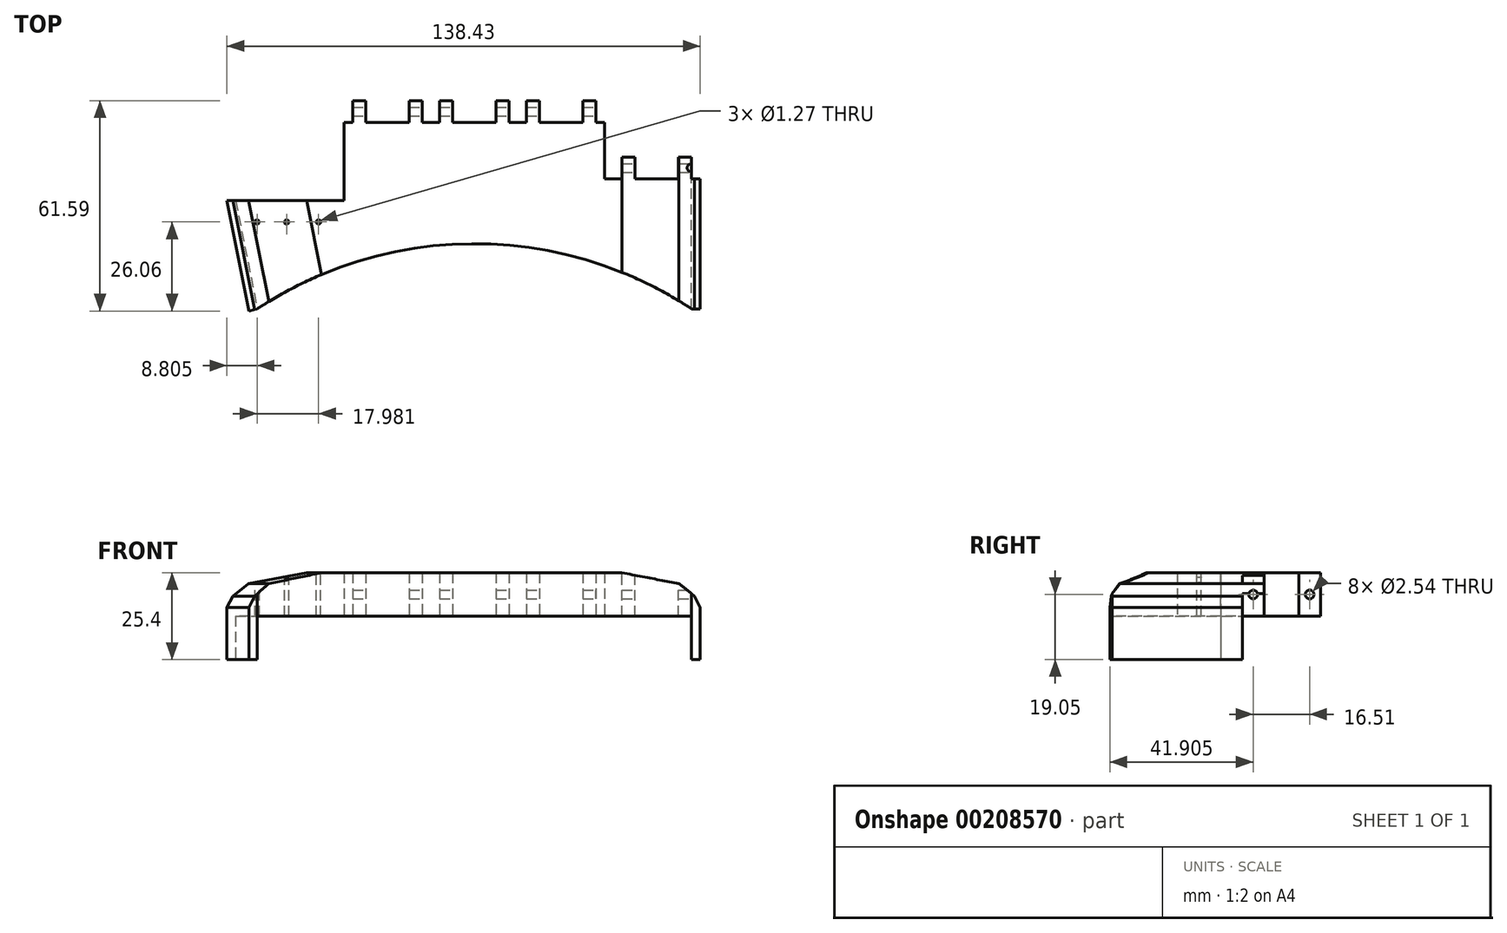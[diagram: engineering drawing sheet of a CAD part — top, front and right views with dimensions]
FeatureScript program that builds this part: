
annotation { "Feature Type Name" : "Feature", "Feature Type Description" : "" }
export const myFeature = defineFeature(function(context is Context, id is Id, definition is map)
    precondition{}
    {
        {
            var Q0;
            Q0=qCreatedBy(makeId("Top.planeOp"),FACE);
            var sketch = newSketch(context, id + "F0", { "sketchPlane" : qUnion([Q0])});
            skArc(sketch, "E0", {"start": v(63.5, 0) * mm, "mid": v(0, 19.05) * mm, "end": v(-63.5, 0) * mm});
            skPoint(sketch, "E1", {"position": v(-38.1, 0) * mm});
            skPoint(sketch, "E2", {"position": v(-38.1, 31.75) * mm});
            skLineSegment(sketch, "E3", {"start": v(-38.1, 31.75) * mm, "end": v(-69.85, 31.75) * mm});
            skLineSegment(sketch, "E4", {"start": v(-69.85, 31.75) * mm, "end": v(-63.5, 0) * mm});
            skLineSegment(sketch, "E5", {"start": v(63.5, 0) * mm, "end": v(63.5, 38.1) * mm});
            skLineSegment(sketch, "E6", {"start": v(63.5, 38.1) * mm, "end": v(38.1, 38.1) * mm});
            skLineSegment(sketch, "E7", {"start": v(38.1, 38.1) * mm, "end": v(38.1, 54.61) * mm});
            skLineSegment(sketch, "E8", {"start": v(38.1, 54.61) * mm, "end": v(-38.1, 54.61) * mm});
            skLineSegment(sketch, "E9", {"start": v(-38.1, 54.61) * mm, "end": v(-38.1, 31.75) * mm});
            skLineSegment(sketch, "E10", {"start": v(-69.85, 31.75) * mm, "end": v(-72.39, 31.75) * mm});
            skLineSegment(sketch, "E11", {"start": v(-72.39, 31.75) * mm, "end": v(-65.91, -0.63) * mm});
            skLineSegment(sketch, "E12", {"start": v(-63.5, 0) * mm, "end": v(-65.91, -0.63) * mm});
            skLineSegment(sketch, "E13", {"start": v(63.5, 38.1) * mm, "end": v(66.04, 38.1) * mm});
            skLineSegment(sketch, "E14", {"start": v(66.04, 0) * mm, "end": v(66.04, 38.1) * mm});
            skLineSegment(sketch, "E15", {"start": v(66.04, 0) * mm, "end": v(63.5, 0) * mm});
            skSolve(sketch);
        }
        {
            var Q0;
            Q0=makeQuery(id+"F0.imprint","IMPRINT",FACE,{"disambiguationData":[TD([[makeQuery(id+"F0.imprint","IMPRINT",EDGE,{"derivedFrom":sQuery(id+"F0.wireOp",EDGE,"E0")}),-1.0]])]});
            extrude(context, id + "F1", {"entities" : qUnion([Q0]), "depth" : 12.7 * mm});
        }
        {
            var Q0;
            Q0=makeQuery(id+"F0.imprint","IMPRINT",FACE,{"disambiguationData":[TD([[makeQuery(id+"F0.imprint","IMPRINT",EDGE,{"derivedFrom":sQuery(id+"F0.wireOp",EDGE,"E4")}),-1.0]])]});
            var Q1;
            Q1=makeQuery(id+"F0.imprint","IMPRINT",FACE,{"disambiguationData":[TD([[makeQuery(id+"F0.imprint","IMPRINT",EDGE,{"derivedFrom":sQuery(id+"F0.wireOp",EDGE,"E5")}),-1.0]])]});
            extrude(context, id + "F2", {"entities" : qUnion([Q0, Q1]), "operationType" : NewBodyOperationType.ADD, "endBound" : BoundingType.SYMMETRIC, "depth" : 25.4 * mm});
        }
        {
            var Q0;
            {var subQ0=sQuery(id+"F0.wireOp",EDGE,"E5");var subQ1=sQuery(id+"F0.wireOp",EDGE,"E4");Q0=makeQuery(id+"F2.boolean.opBoolean","MERGE",FACE,{"derivedFrom":[makeQuery(id+"F1.opExtrude","CAP_FACE",FACE,{"disambiguationData":[OSD([sQuery(id+"F0.wireOp",EDGE,"E0"),sQuery(id+"F0.wireOp",EDGE,"E3"),subQ1,subQ0,sQuery(id+"F0.wireOp",EDGE,"E6"),sQuery(id+"F0.wireOp",EDGE,"E7"),sQuery(id+"F0.wireOp",EDGE,"E8"),sQuery(id+"F0.wireOp",EDGE,"E9")])],"isStart":false}),makeQuery(id+"F2.opExtrude","CAP_FACE",FACE,{"disambiguationData":[OSD([subQ1,sQuery(id+"F0.wireOp",EDGE,"E10"),sQuery(id+"F0.wireOp",EDGE,"E11"),sQuery(id+"F0.wireOp",EDGE,"E12")])],"isStart":false}),makeQuery(id+"F2.opExtrude","CAP_FACE",FACE,{"disambiguationData":[OSD([subQ0,sQuery(id+"F0.wireOp",EDGE,"E13"),sQuery(id+"F0.wireOp",EDGE,"E14"),sQuery(id+"F0.wireOp",EDGE,"E15")])],"isStart":false})]});}
            var sketch = newSketch(context, id + "F3", { "sketchPlane" : qUnion([Q0])});
            skPoint(sketch, "E16", {"position": v(-63.58, 25.43) * mm});
            skPoint(sketch, "E17", {"position": v(-54.92, 25.43) * mm});
            skPoint(sketch, "E18", {"position": v(-45.6, 25.43) * mm});
            skLineSegment(sketch, "E19", {"start": v(-12.7, 54.61) * mm, "end": v(-12.7, 41.78) * mm});
            skLineSegment(sketch, "E20", {"start": v(12.7, 54.61) * mm, "end": v(12.7, 42.32) * mm});
            skLineSegment(sketch, "E21.bottom", {"start": v(-35.56, 54.61) * mm, "end": v(-30.48, 54.61) * mm});
            skLineSegment(sketch, "E21.top", {"start": v(-35.56, 44.45) * mm, "end": v(-30.48, 44.45) * mm});
            skLineSegment(sketch, "E21.left", {"start": v(-35.56, 54.61) * mm, "end": v(-35.56, 44.45) * mm});
            skLineSegment(sketch, "E21.right", {"start": v(-30.48, 54.61) * mm, "end": v(-30.48, 44.45) * mm});
            skLineSegment(sketch, "E22.bottom", {"start": v(-20.32, 54.61) * mm, "end": v(-15.24, 54.61) * mm});
            skLineSegment(sketch, "E22.top", {"start": v(-20.32, 44.45) * mm, "end": v(-15.24, 44.45) * mm});
            skLineSegment(sketch, "E22.left", {"start": v(-20.32, 54.61) * mm, "end": v(-20.32, 44.45) * mm});
            skLineSegment(sketch, "E22.right", {"start": v(-15.24, 54.61) * mm, "end": v(-15.24, 44.45) * mm});
            skLineSegment(sketch, "E23.MirrorCS", {"start": v(-5.08, 54.61) * mm, "end": v(-10.16, 54.61) * mm});
            skLineSegment(sketch, "E24.MirrorCS", {"start": v(-5.08, 44.45) * mm, "end": v(-10.16, 44.45) * mm});
            skLineSegment(sketch, "E25.MirrorCS", {"start": v(-5.08, 54.61) * mm, "end": v(-5.08, 44.45) * mm});
            skLineSegment(sketch, "E26.MirrorCS", {"start": v(5.08, 54.61) * mm, "end": v(5.08, 44.45) * mm});
            skLineSegment(sketch, "E27.MirrorCS", {"start": v(10.16, 54.61) * mm, "end": v(10.16, 44.45) * mm});
            skLineSegment(sketch, "E28.MirrorCS", {"start": v(10.16, 54.61) * mm, "end": v(5.08, 54.61) * mm});
            skLineSegment(sketch, "E29.MirrorCS", {"start": v(-10.16, 54.61) * mm, "end": v(-10.16, 44.45) * mm});
            skLineSegment(sketch, "E30.MirrorCS", {"start": v(10.16, 44.45) * mm, "end": v(5.08, 44.45) * mm});
            skLineSegment(sketch, "E31.MirrorCS", {"start": v(35.56, 54.61) * mm, "end": v(35.56, 44.45) * mm});
            skLineSegment(sketch, "E32.MirrorCS", {"start": v(30.48, 54.61) * mm, "end": v(30.48, 44.45) * mm});
            skLineSegment(sketch, "E33.MirrorCS", {"start": v(30.48, 44.45) * mm, "end": v(35.56, 44.45) * mm});
            skLineSegment(sketch, "E34.MirrorCS", {"start": v(15.24, 44.45) * mm, "end": v(20.32, 44.45) * mm});
            skLineSegment(sketch, "E35.MirrorCS", {"start": v(15.24, 54.61) * mm, "end": v(20.32, 54.61) * mm});
            skLineSegment(sketch, "E36.MirrorCS", {"start": v(20.32, 54.61) * mm, "end": v(20.32, 44.45) * mm});
            skLineSegment(sketch, "E37.MirrorCS", {"start": v(30.48, 54.61) * mm, "end": v(35.56, 54.61) * mm});
            skLineSegment(sketch, "E38.MirrorCS", {"start": v(15.24, 54.61) * mm, "end": v(15.24, 44.45) * mm});
            skLineSegment(sketch, "E39.MirrorCS", {"start": v(66.04, 38.1) * mm, "end": v(66.04, 27.94) * mm});
            skLineSegment(sketch, "E40.MirrorCS", {"start": v(60.96, 38.1) * mm, "end": v(60.96, 27.94) * mm});
            skLineSegment(sketch, "E41.MirrorCS", {"start": v(60.96, 27.94) * mm, "end": v(66.04, 27.94) * mm});
            skLineSegment(sketch, "E42.MirrorCS", {"start": v(45.72, 27.94) * mm, "end": v(50.8, 27.94) * mm});
            skLineSegment(sketch, "E43.MirrorCS", {"start": v(45.72, 38.1) * mm, "end": v(50.8, 38.1) * mm});
            skLineSegment(sketch, "E44.MirrorCS", {"start": v(50.8, 38.1) * mm, "end": v(50.8, 27.94) * mm});
            skLineSegment(sketch, "E45.MirrorCS", {"start": v(60.96, 38.1) * mm, "end": v(66.04, 38.1) * mm});
            skLineSegment(sketch, "E46.MirrorCS", {"start": v(45.72, 38.1) * mm, "end": v(45.72, 27.94) * mm});
            skSolve(sketch);
        }
        {
            var Q0;
            Q0=sQuery(id+"F3.wireOp",VERTEX,"E18");
            var Q1;
            Q1=sQuery(id+"F3.wireOp",VERTEX,"E17");
            var Q2;
            Q2=sQuery(id+"F3.wireOp",VERTEX,"E16");
            var Q3;
            Q3=makeQuery(id+"F1.opExtrude","SWEPT_BODY",BODY,{"disambiguationData":[OSD([sQuery(id+"F0.wireOp",EDGE,"E0"),sQuery(id+"F0.wireOp",EDGE,"E3"),sQuery(id+"F0.wireOp",EDGE,"E4"),sQuery(id+"F0.wireOp",EDGE,"E5"),sQuery(id+"F0.wireOp",EDGE,"E6"),sQuery(id+"F0.wireOp",EDGE,"E7"),sQuery(id+"F0.wireOp",EDGE,"E8"),sQuery(id+"F0.wireOp",EDGE,"E9")])]});
            hole(context, id + "F4", {"style" : HoleStyle.SIMPLE, "endStyle" : HoleEndStyle.THROUGH, "holeDiameter" : 1.27 * mm, "locations" : qUnion([Q0, Q1, Q2]), "scope" : qUnion([Q3]), "isTappedThrough" : true});
        }
        {
            var Q0;
            Q0=makeQuery(id+"F1.opExtrude","SWEPT_FACE",FACE,{"disambiguationData":[OSD([sQuery(id+"F0.wireOp",EDGE,"E8")])]});
            var sketch = newSketch(context, id + "F5", { "sketchPlane" : qUnion([Q0])});
            skLineSegment(sketch, "E47", {"start": v(12.7, 12.7) * mm, "end": v(12.7, 0) * mm});
            skLineSegment(sketch, "E48", {"start": v(-12.7, 12.7) * mm, "end": v(-12.7, 0) * mm});
            skLineSegment(sketch, "E49.bottom", {"start": v(-35.56, 12.7) * mm, "end": v(-31.75, 12.7) * mm});
            skLineSegment(sketch, "E49.top", {"start": v(-35.56, 0) * mm, "end": v(-31.75, 0) * mm});
            skLineSegment(sketch, "E49.left", {"start": v(-35.56, 12.7) * mm, "end": v(-35.56, 0) * mm});
            skLineSegment(sketch, "E49.right", {"start": v(-31.75, 12.7) * mm, "end": v(-31.75, 0) * mm});
            skLineSegment(sketch, "E50.bottom", {"start": v(-19.05, 12.7) * mm, "end": v(-15.24, 12.7) * mm});
            skLineSegment(sketch, "E50.top", {"start": v(-19.05, 0) * mm, "end": v(-15.24, 0) * mm});
            skLineSegment(sketch, "E50.left", {"start": v(-19.05, 12.7) * mm, "end": v(-19.05, 0) * mm});
            skLineSegment(sketch, "E50.right", {"start": v(-15.24, 12.7) * mm, "end": v(-15.24, 0) * mm});
            skLineSegment(sketch, "E51.MirrorCS", {"start": v(-6.35, 12.7) * mm, "end": v(-10.16, 12.7) * mm});
            skLineSegment(sketch, "E52.MirrorCS", {"start": v(10.16, 12.7) * mm, "end": v(6.35, 12.7) * mm});
            skLineSegment(sketch, "E53.MirrorCS", {"start": v(-6.35, 0) * mm, "end": v(-10.16, 0) * mm});
            skLineSegment(sketch, "E54.MirrorCS", {"start": v(10.16, 0) * mm, "end": v(6.35, 0) * mm});
            skLineSegment(sketch, "E55.MirrorCS", {"start": v(-6.35, 12.7) * mm, "end": v(-6.35, 0) * mm});
            skLineSegment(sketch, "E56.MirrorCS", {"start": v(10.16, 12.7) * mm, "end": v(10.16, 0) * mm});
            skLineSegment(sketch, "E57.MirrorCS", {"start": v(6.35, 12.7) * mm, "end": v(6.35, 0) * mm});
            skLineSegment(sketch, "E58.MirrorCS", {"start": v(-10.16, 12.7) * mm, "end": v(-10.16, 0) * mm});
            skLineSegment(sketch, "E59.MirrorCS", {"start": v(31.75, 0) * mm, "end": v(35.56, 0) * mm});
            skLineSegment(sketch, "E60.MirrorCS", {"start": v(15.24, 12.7) * mm, "end": v(19.05, 12.7) * mm});
            skLineSegment(sketch, "E61.MirrorCS", {"start": v(31.75, 12.7) * mm, "end": v(35.56, 12.7) * mm});
            skLineSegment(sketch, "E62.MirrorCS", {"start": v(15.24, 12.7) * mm, "end": v(15.24, 0) * mm});
            skLineSegment(sketch, "E63.MirrorCS", {"start": v(31.75, 12.7) * mm, "end": v(31.75, 0) * mm});
            skLineSegment(sketch, "E64.MirrorCS", {"start": v(15.24, 0) * mm, "end": v(19.05, 0) * mm});
            skLineSegment(sketch, "E65.MirrorCS", {"start": v(19.05, 12.7) * mm, "end": v(19.05, 0) * mm});
            skLineSegment(sketch, "E66.MirrorCS", {"start": v(35.56, 12.7) * mm, "end": v(35.56, 0) * mm});
            skSolve(sketch);
        }
        {
            var Q0;
            Q0=makeQuery(id+"F5.imprint","IMPRINT",FACE,{"disambiguationData":[TD([[makeQuery(id+"F5.imprint","IMPRINT",EDGE,{"derivedFrom":sQuery(id+"F5.wireOp",EDGE,"E49.bottom")}),-1.0]])]});
            var Q1;
            Q1=makeQuery(id+"F5.imprint","IMPRINT",FACE,{"disambiguationData":[TD([[makeQuery(id+"F5.imprint","IMPRINT",EDGE,{"derivedFrom":sQuery(id+"F5.wireOp",EDGE,"E50.bottom")}),-1.0]])]});
            var Q2;
            Q2=makeQuery(id+"F5.imprint","IMPRINT",FACE,{"disambiguationData":[TD([[makeQuery(id+"F5.imprint","IMPRINT",EDGE,{"derivedFrom":sQuery(id+"F5.wireOp",EDGE,"E51.MirrorCS")}),-1.0]])]});
            var Q3;
            Q3=makeQuery(id+"F5.imprint","IMPRINT",FACE,{"disambiguationData":[TD([[makeQuery(id+"F5.imprint","IMPRINT",EDGE,{"derivedFrom":sQuery(id+"F5.wireOp",EDGE,"E52.MirrorCS")}),-1.0]])]});
            var Q4;
            Q4=makeQuery(id+"F5.imprint","IMPRINT",FACE,{"disambiguationData":[TD([[makeQuery(id+"F5.imprint","IMPRINT",EDGE,{"derivedFrom":sQuery(id+"F5.wireOp",EDGE,"E60.MirrorCS")}),-1.0]])]});
            var Q5;
            Q5=makeQuery(id+"F5.imprint","IMPRINT",FACE,{"disambiguationData":[TD([[makeQuery(id+"F5.imprint","IMPRINT",EDGE,{"derivedFrom":sQuery(id+"F5.wireOp",EDGE,"E59.MirrorCS")}),1.0]])]});
            extrude(context, id + "F6", {"entities" : qUnion([Q0, Q1, Q2, Q3, Q4, Q5]), "operationType" : NewBodyOperationType.ADD, "depth" : 6.35 * mm});
        }
        {
            var Q0;
            Q0=makeQuery(id+"F6.opExtrude","SWEPT_FACE",FACE,{"disambiguationData":[OSD([sQuery(id+"F5.wireOp",EDGE,"E49.left")])]});
            var sketch = newSketch(context, id + "F7", { "sketchPlane" : qUnion([Q0])});
            skPoint(sketch, "E67", {"position": v(57.79, 6.35) * mm});
            skPoint(sketch, "E67.positionSnap0", {"position": v(60.96, 6.35) * mm});
            skPoint(sketch, "E67.positionSnap1", {"position": v(57.79, 12.7) * mm});
            skSolve(sketch);
        }
        {
            var Q0;
            Q0=sQuery(id+"F7.wireOp",VERTEX,"E67");
            var Q1;
            Q1=makeQuery(id+"F1.opExtrude","SWEPT_BODY",BODY,{"disambiguationData":[OSD([sQuery(id+"F0.wireOp",EDGE,"E0"),sQuery(id+"F0.wireOp",EDGE,"E3"),sQuery(id+"F0.wireOp",EDGE,"E4"),sQuery(id+"F0.wireOp",EDGE,"E5"),sQuery(id+"F0.wireOp",EDGE,"E6"),sQuery(id+"F0.wireOp",EDGE,"E7"),sQuery(id+"F0.wireOp",EDGE,"E8"),sQuery(id+"F0.wireOp",EDGE,"E9")])]});
            hole(context, id + "F8", {"style" : HoleStyle.SIMPLE, "endStyle" : HoleEndStyle.THROUGH, "holeDiameter" : 2.54 * mm, "locations" : qUnion([Q0]), "scope" : qUnion([Q1]), "isTappedThrough" : true});
        }
        {
            var Q0;
            Q0=makeQuery(id+"F2.boolean.opBoolean","MERGE",FACE,{"derivedFrom":[makeQuery(id+"F1.opExtrude","SWEPT_FACE",FACE,{"disambiguationData":[OSD([sQuery(id+"F0.wireOp",EDGE,"E6")])]}),makeQuery(id+"F2.opExtrude","SWEPT_FACE",FACE,{"disambiguationData":[OSD([sQuery(id+"F0.wireOp",EDGE,"E13")])]})]});
            var sketch = newSketch(context, id + "F9", { "sketchPlane" : qUnion([Q0])});
            skLineSegment(sketch, "E68.bottom", {"start": v(-63.5, 0) * mm, "end": v(-59.7, 0) * mm});
            skLineSegment(sketch, "E68.top", {"start": v(-63.5, 12.7) * mm, "end": v(-59.7, 12.7) * mm});
            skLineSegment(sketch, "E68.left", {"start": v(-63.5, 0) * mm, "end": v(-63.5, 12.7) * mm});
            skLineSegment(sketch, "E68.right", {"start": v(-59.7, 0) * mm, "end": v(-59.7, 12.7) * mm});
            skLineSegment(sketch, "E69.bottom", {"start": v(-43.18, 0) * mm, "end": v(-47, 0) * mm});
            skLineSegment(sketch, "E69.top", {"start": v(-43.18, 12.7) * mm, "end": v(-47, 12.7) * mm});
            skLineSegment(sketch, "E69.left", {"start": v(-43.18, 0) * mm, "end": v(-43.18, 12.7) * mm});
            skLineSegment(sketch, "E69.right", {"start": v(-47, 0) * mm, "end": v(-47, 12.7) * mm});
            skSolve(sketch);
        }
        {
            var Q0;
            Q0=makeQuery(id+"F9.imprint","IMPRINT",FACE,{"disambiguationData":[TD([[makeQuery(id+"F9.imprint","IMPRINT",EDGE,{"derivedFrom":sQuery(id+"F9.wireOp",EDGE,"E69.bottom")}),1.0]])]});
            var Q1;
            Q1=makeQuery(id+"F9.imprint","IMPRINT",FACE,{"disambiguationData":[TD([[makeQuery(id+"F9.imprint","IMPRINT",EDGE,{"derivedFrom":sQuery(id+"F9.wireOp",EDGE,"E68.bottom")}),1.0]])]});
            extrude(context, id + "F10", {"entities" : qUnion([Q0, Q1]), "operationType" : NewBodyOperationType.ADD, "depth" : 6.35 * mm});
        }
        {
            var Q0;
            Q0=makeQuery(id+"F10.opExtrude","SWEPT_FACE",FACE,{"disambiguationData":[OSD([sQuery(id+"F9.wireOp",EDGE,"E68.left")])]});
            var sketch = newSketch(context, id + "F11", { "sketchPlane" : qUnion([Q0])});
            skPoint(sketch, "E70", {"position": v(41.28, 6.35) * mm});
            skPoint(sketch, "E70.positionSnap0", {"position": v(44.45, 6.35) * mm});
            skPoint(sketch, "E70.positionSnap1", {"position": v(41.28, 12.7) * mm});
            skSolve(sketch);
        }
        {
            var Q0;
            Q0=sQuery(id+"F11.wireOp",VERTEX,"E70");
            var Q1;
            Q1=makeQuery(id+"F1.opExtrude","SWEPT_BODY",BODY,{"disambiguationData":[OSD([sQuery(id+"F0.wireOp",EDGE,"E0"),sQuery(id+"F0.wireOp",EDGE,"E3"),sQuery(id+"F0.wireOp",EDGE,"E4"),sQuery(id+"F0.wireOp",EDGE,"E5"),sQuery(id+"F0.wireOp",EDGE,"E6"),sQuery(id+"F0.wireOp",EDGE,"E7"),sQuery(id+"F0.wireOp",EDGE,"E8"),sQuery(id+"F0.wireOp",EDGE,"E9")])]});
            hole(context, id + "F12", {"style" : HoleStyle.SIMPLE, "endStyle" : HoleEndStyle.BLIND, "holeDiameter" : 2.54 * mm, "holeDepth" : 22.86 * mm, "locations" : qUnion([Q0]), "scope" : qUnion([Q1])});
        }
        {
            var Q0;
            Q0=makeQuery(id+"F2.opExtrude","CAP_EDGE",EDGE,{"disambiguationData":[OSD([sQuery(id+"F0.wireOp",EDGE,"E14")])],"isStart":false});
            var Q1;
            Q1=makeQuery(id+"F2.opExtrude","CAP_EDGE",EDGE,{"disambiguationData":[OSD([sQuery(id+"F0.wireOp",EDGE,"E11")])],"isStart":false});
            chamfer(context, id + "F13", {"entities" : qUnion([Q0, Q1]), "chamferType" : ChamferType.TWO_OFFSETS, "width1" : 5.08 * mm, "oppositeDirection" : false, "width2" : 10.16 * mm, "tangentPropagation" : true});
        }
        {
            var Q0;
            {var subQ0=sQuery(id+"F0.wireOp",EDGE,"E5");var subQ1=sQuery(id+"F0.wireOp",EDGE,"E11");var subQ2=sQuery(id+"F0.wireOp",EDGE,"E4");Q0=makeQuery(id+"F13.opChamfer","BLEND_EDGE",EDGE,{"blendedFrom":[makeQuery(id+"F2.opExtrude","CAP_EDGE",EDGE,{"disambiguationData":[OSD([subQ1])],"isStart":false}),makeQuery(id+"F10.boolean.opBoolean","MERGE",FACE,{"derivedFrom":[makeQuery(id+"F6.boolean.opBoolean","MERGE",FACE,{"derivedFrom":[makeQuery(id+"F2.boolean.opBoolean","MERGE",FACE,{"derivedFrom":[makeQuery(id+"F1.opExtrude","CAP_FACE",FACE,{"disambiguationData":[OSD([sQuery(id+"F0.wireOp",EDGE,"E0"),sQuery(id+"F0.wireOp",EDGE,"E3"),subQ2,subQ0,sQuery(id+"F0.wireOp",EDGE,"E6"),sQuery(id+"F0.wireOp",EDGE,"E7"),sQuery(id+"F0.wireOp",EDGE,"E8"),sQuery(id+"F0.wireOp",EDGE,"E9")])],"isStart":false}),makeQuery(id+"F2.opExtrude","CAP_FACE",FACE,{"disambiguationData":[OSD([subQ2,sQuery(id+"F0.wireOp",EDGE,"E10"),subQ1,sQuery(id+"F0.wireOp",EDGE,"E12")])],"isStart":false}),makeQuery(id+"F2.opExtrude","CAP_FACE",FACE,{"disambiguationData":[OSD([subQ0,sQuery(id+"F0.wireOp",EDGE,"E13"),sQuery(id+"F0.wireOp",EDGE,"E14"),sQuery(id+"F0.wireOp",EDGE,"E15")])],"isStart":false})]}),makeQuery(id+"F6.opExtrude","SWEPT_FACE",FACE,{"disambiguationData":[OSD([sQuery(id+"F5.wireOp",EDGE,"E49.bottom")])]}),makeQuery(id+"F6.opExtrude","SWEPT_FACE",FACE,{"disambiguationData":[OSD([sQuery(id+"F5.wireOp",EDGE,"E50.bottom")])]}),makeQuery(id+"F6.opExtrude","SWEPT_FACE",FACE,{"disambiguationData":[OSD([sQuery(id+"F5.wireOp",EDGE,"E51.MirrorCS")])]}),makeQuery(id+"F6.opExtrude","SWEPT_FACE",FACE,{"disambiguationData":[OSD([sQuery(id+"F5.wireOp",EDGE,"E52.MirrorCS")])]}),makeQuery(id+"F6.opExtrude","SWEPT_FACE",FACE,{"disambiguationData":[OSD([sQuery(id+"F5.wireOp",EDGE,"E60.MirrorCS")])]}),makeQuery(id+"F6.opExtrude","SWEPT_FACE",FACE,{"disambiguationData":[OSD([sQuery(id+"F5.wireOp",EDGE,"E61.MirrorCS")])]})]}),makeQuery(id+"F10.opExtrude","SWEPT_FACE",FACE,{"disambiguationData":[OSD([sQuery(id+"F9.wireOp",EDGE,"E68.top")])]}),makeQuery(id+"F10.opExtrude","SWEPT_FACE",FACE,{"disambiguationData":[OSD([sQuery(id+"F9.wireOp",EDGE,"E69.top")])]})]})],"blendedInto":[makeQuery(id+"F10.boolean.opBoolean","MERGE",FACE,{"derivedFrom":[makeQuery(id+"F6.boolean.opBoolean","MERGE",FACE,{"derivedFrom":[makeQuery(id+"F2.boolean.opBoolean","MERGE",FACE,{"derivedFrom":[makeQuery(id+"F1.opExtrude","CAP_FACE",FACE,{"disambiguationData":[OSD([sQuery(id+"F0.wireOp",EDGE,"E0"),sQuery(id+"F0.wireOp",EDGE,"E3"),subQ2,subQ0,sQuery(id+"F0.wireOp",EDGE,"E6"),sQuery(id+"F0.wireOp",EDGE,"E7"),sQuery(id+"F0.wireOp",EDGE,"E8"),sQuery(id+"F0.wireOp",EDGE,"E9")])],"isStart":false}),makeQuery(id+"F2.opExtrude","CAP_FACE",FACE,{"disambiguationData":[OSD([subQ2,sQuery(id+"F0.wireOp",EDGE,"E10"),subQ1,sQuery(id+"F0.wireOp",EDGE,"E12")])],"isStart":false}),makeQuery(id+"F2.opExtrude","CAP_FACE",FACE,{"disambiguationData":[OSD([subQ0,sQuery(id+"F0.wireOp",EDGE,"E13"),sQuery(id+"F0.wireOp",EDGE,"E14"),sQuery(id+"F0.wireOp",EDGE,"E15")])],"isStart":false})]}),makeQuery(id+"F6.opExtrude","SWEPT_FACE",FACE,{"disambiguationData":[OSD([sQuery(id+"F5.wireOp",EDGE,"E49.bottom")])]}),makeQuery(id+"F6.opExtrude","SWEPT_FACE",FACE,{"disambiguationData":[OSD([sQuery(id+"F5.wireOp",EDGE,"E50.bottom")])]}),makeQuery(id+"F6.opExtrude","SWEPT_FACE",FACE,{"disambiguationData":[OSD([sQuery(id+"F5.wireOp",EDGE,"E51.MirrorCS")])]}),makeQuery(id+"F6.opExtrude","SWEPT_FACE",FACE,{"disambiguationData":[OSD([sQuery(id+"F5.wireOp",EDGE,"E52.MirrorCS")])]}),makeQuery(id+"F6.opExtrude","SWEPT_FACE",FACE,{"disambiguationData":[OSD([sQuery(id+"F5.wireOp",EDGE,"E60.MirrorCS")])]}),makeQuery(id+"F6.opExtrude","SWEPT_FACE",FACE,{"disambiguationData":[OSD([sQuery(id+"F5.wireOp",EDGE,"E61.MirrorCS")])]})]}),makeQuery(id+"F10.opExtrude","SWEPT_FACE",FACE,{"disambiguationData":[OSD([sQuery(id+"F9.wireOp",EDGE,"E68.top")])]}),makeQuery(id+"F10.opExtrude","SWEPT_FACE",FACE,{"disambiguationData":[OSD([sQuery(id+"F9.wireOp",EDGE,"E69.top")])]})]})]});}
            var Q1;
            {var subQ0=sQuery(id+"F0.wireOp",EDGE,"E14");var subQ1=sQuery(id+"F0.wireOp",EDGE,"E5");var subQ2=sQuery(id+"F0.wireOp",EDGE,"E4");Q1=makeQuery(id+"F13.opChamfer","BLEND_EDGE",EDGE,{"blendedFrom":[makeQuery(id+"F2.opExtrude","CAP_EDGE",EDGE,{"disambiguationData":[OSD([subQ0])],"isStart":false}),makeQuery(id+"F10.boolean.opBoolean","MERGE",FACE,{"derivedFrom":[makeQuery(id+"F6.boolean.opBoolean","MERGE",FACE,{"derivedFrom":[makeQuery(id+"F2.boolean.opBoolean","MERGE",FACE,{"derivedFrom":[makeQuery(id+"F1.opExtrude","CAP_FACE",FACE,{"disambiguationData":[OSD([sQuery(id+"F0.wireOp",EDGE,"E0"),sQuery(id+"F0.wireOp",EDGE,"E3"),subQ2,subQ1,sQuery(id+"F0.wireOp",EDGE,"E6"),sQuery(id+"F0.wireOp",EDGE,"E7"),sQuery(id+"F0.wireOp",EDGE,"E8"),sQuery(id+"F0.wireOp",EDGE,"E9")])],"isStart":false}),makeQuery(id+"F2.opExtrude","CAP_FACE",FACE,{"disambiguationData":[OSD([subQ2,sQuery(id+"F0.wireOp",EDGE,"E10"),sQuery(id+"F0.wireOp",EDGE,"E11"),sQuery(id+"F0.wireOp",EDGE,"E12")])],"isStart":false}),makeQuery(id+"F2.opExtrude","CAP_FACE",FACE,{"disambiguationData":[OSD([subQ1,sQuery(id+"F0.wireOp",EDGE,"E13"),subQ0,sQuery(id+"F0.wireOp",EDGE,"E15")])],"isStart":false})]}),makeQuery(id+"F6.opExtrude","SWEPT_FACE",FACE,{"disambiguationData":[OSD([sQuery(id+"F5.wireOp",EDGE,"E49.bottom")])]}),makeQuery(id+"F6.opExtrude","SWEPT_FACE",FACE,{"disambiguationData":[OSD([sQuery(id+"F5.wireOp",EDGE,"E50.bottom")])]}),makeQuery(id+"F6.opExtrude","SWEPT_FACE",FACE,{"disambiguationData":[OSD([sQuery(id+"F5.wireOp",EDGE,"E51.MirrorCS")])]}),makeQuery(id+"F6.opExtrude","SWEPT_FACE",FACE,{"disambiguationData":[OSD([sQuery(id+"F5.wireOp",EDGE,"E52.MirrorCS")])]}),makeQuery(id+"F6.opExtrude","SWEPT_FACE",FACE,{"disambiguationData":[OSD([sQuery(id+"F5.wireOp",EDGE,"E60.MirrorCS")])]}),makeQuery(id+"F6.opExtrude","SWEPT_FACE",FACE,{"disambiguationData":[OSD([sQuery(id+"F5.wireOp",EDGE,"E61.MirrorCS")])]})]}),makeQuery(id+"F10.opExtrude","SWEPT_FACE",FACE,{"disambiguationData":[OSD([sQuery(id+"F9.wireOp",EDGE,"E68.top")])]}),makeQuery(id+"F10.opExtrude","SWEPT_FACE",FACE,{"disambiguationData":[OSD([sQuery(id+"F9.wireOp",EDGE,"E69.top")])]})]})],"blendedInto":[makeQuery(id+"F10.boolean.opBoolean","MERGE",FACE,{"derivedFrom":[makeQuery(id+"F6.boolean.opBoolean","MERGE",FACE,{"derivedFrom":[makeQuery(id+"F2.boolean.opBoolean","MERGE",FACE,{"derivedFrom":[makeQuery(id+"F1.opExtrude","CAP_FACE",FACE,{"disambiguationData":[OSD([sQuery(id+"F0.wireOp",EDGE,"E0"),sQuery(id+"F0.wireOp",EDGE,"E3"),subQ2,subQ1,sQuery(id+"F0.wireOp",EDGE,"E6"),sQuery(id+"F0.wireOp",EDGE,"E7"),sQuery(id+"F0.wireOp",EDGE,"E8"),sQuery(id+"F0.wireOp",EDGE,"E9")])],"isStart":false}),makeQuery(id+"F2.opExtrude","CAP_FACE",FACE,{"disambiguationData":[OSD([subQ2,sQuery(id+"F0.wireOp",EDGE,"E10"),sQuery(id+"F0.wireOp",EDGE,"E11"),sQuery(id+"F0.wireOp",EDGE,"E12")])],"isStart":false}),makeQuery(id+"F2.opExtrude","CAP_FACE",FACE,{"disambiguationData":[OSD([subQ1,sQuery(id+"F0.wireOp",EDGE,"E13"),subQ0,sQuery(id+"F0.wireOp",EDGE,"E15")])],"isStart":false})]}),makeQuery(id+"F6.opExtrude","SWEPT_FACE",FACE,{"disambiguationData":[OSD([sQuery(id+"F5.wireOp",EDGE,"E49.bottom")])]}),makeQuery(id+"F6.opExtrude","SWEPT_FACE",FACE,{"disambiguationData":[OSD([sQuery(id+"F5.wireOp",EDGE,"E50.bottom")])]}),makeQuery(id+"F6.opExtrude","SWEPT_FACE",FACE,{"disambiguationData":[OSD([sQuery(id+"F5.wireOp",EDGE,"E51.MirrorCS")])]}),makeQuery(id+"F6.opExtrude","SWEPT_FACE",FACE,{"disambiguationData":[OSD([sQuery(id+"F5.wireOp",EDGE,"E52.MirrorCS")])]}),makeQuery(id+"F6.opExtrude","SWEPT_FACE",FACE,{"disambiguationData":[OSD([sQuery(id+"F5.wireOp",EDGE,"E60.MirrorCS")])]}),makeQuery(id+"F6.opExtrude","SWEPT_FACE",FACE,{"disambiguationData":[OSD([sQuery(id+"F5.wireOp",EDGE,"E61.MirrorCS")])]})]}),makeQuery(id+"F10.opExtrude","SWEPT_FACE",FACE,{"disambiguationData":[OSD([sQuery(id+"F9.wireOp",EDGE,"E68.top")])]}),makeQuery(id+"F10.opExtrude","SWEPT_FACE",FACE,{"disambiguationData":[OSD([sQuery(id+"F9.wireOp",EDGE,"E69.top")])]})]})]});}
            chamfer(context, id + "F14", {"entities" : qUnion([Q0, Q1]), "chamferType" : ChamferType.TWO_OFFSETS, "width1" : 5.08 * mm, "oppositeDirection" : false, "width2" : 7.62 * mm, "tangentPropagation" : true});
        }
        {
            var Q0;
            {var subQ0=sQuery(id+"F0.wireOp",EDGE,"E5");var subQ1=sQuery(id+"F0.wireOp",EDGE,"E11");var subQ2=sQuery(id+"F0.wireOp",EDGE,"E4");var subQ3=makeQuery(id+"F10.boolean.opBoolean","MERGE",FACE,{"derivedFrom":[makeQuery(id+"F6.boolean.opBoolean","MERGE",FACE,{"derivedFrom":[makeQuery(id+"F2.boolean.opBoolean","MERGE",FACE,{"derivedFrom":[makeQuery(id+"F1.opExtrude","CAP_FACE",FACE,{"disambiguationData":[OSD([sQuery(id+"F0.wireOp",EDGE,"E0"),sQuery(id+"F0.wireOp",EDGE,"E3"),subQ2,subQ0,sQuery(id+"F0.wireOp",EDGE,"E6"),sQuery(id+"F0.wireOp",EDGE,"E7"),sQuery(id+"F0.wireOp",EDGE,"E8"),sQuery(id+"F0.wireOp",EDGE,"E9")])],"isStart":false}),makeQuery(id+"F2.opExtrude","CAP_FACE",FACE,{"disambiguationData":[OSD([subQ2,sQuery(id+"F0.wireOp",EDGE,"E10"),subQ1,sQuery(id+"F0.wireOp",EDGE,"E12")])],"isStart":false}),makeQuery(id+"F2.opExtrude","CAP_FACE",FACE,{"disambiguationData":[OSD([subQ0,sQuery(id+"F0.wireOp",EDGE,"E13"),sQuery(id+"F0.wireOp",EDGE,"E14"),sQuery(id+"F0.wireOp",EDGE,"E15")])],"isStart":false})]}),makeQuery(id+"F6.opExtrude","SWEPT_FACE",FACE,{"disambiguationData":[OSD([sQuery(id+"F5.wireOp",EDGE,"E49.bottom")])]}),makeQuery(id+"F6.opExtrude","SWEPT_FACE",FACE,{"disambiguationData":[OSD([sQuery(id+"F5.wireOp",EDGE,"E50.bottom")])]}),makeQuery(id+"F6.opExtrude","SWEPT_FACE",FACE,{"disambiguationData":[OSD([sQuery(id+"F5.wireOp",EDGE,"E51.MirrorCS")])]}),makeQuery(id+"F6.opExtrude","SWEPT_FACE",FACE,{"disambiguationData":[OSD([sQuery(id+"F5.wireOp",EDGE,"E52.MirrorCS")])]}),makeQuery(id+"F6.opExtrude","SWEPT_FACE",FACE,{"disambiguationData":[OSD([sQuery(id+"F5.wireOp",EDGE,"E60.MirrorCS")])]}),makeQuery(id+"F6.opExtrude","SWEPT_FACE",FACE,{"disambiguationData":[OSD([sQuery(id+"F5.wireOp",EDGE,"E61.MirrorCS")])]})]}),makeQuery(id+"F10.opExtrude","SWEPT_FACE",FACE,{"disambiguationData":[OSD([sQuery(id+"F9.wireOp",EDGE,"E68.top")])]}),makeQuery(id+"F10.opExtrude","SWEPT_FACE",FACE,{"disambiguationData":[OSD([sQuery(id+"F9.wireOp",EDGE,"E69.top")])]})]});Q0=makeQuery(id+"F14.opChamfer","BLEND_EDGE",EDGE,{"blendedFrom":[makeQuery(id+"F13.opChamfer","BLEND_EDGE",EDGE,{"blendedFrom":[makeQuery(id+"F2.opExtrude","CAP_EDGE",EDGE,{"disambiguationData":[OSD([subQ1])],"isStart":false}),subQ3],"blendedInto":[subQ3]}),subQ3],"blendedInto":[subQ3]});}
            var Q1;
            {var subQ0=sQuery(id+"F0.wireOp",EDGE,"E14");var subQ1=sQuery(id+"F0.wireOp",EDGE,"E5");var subQ2=sQuery(id+"F0.wireOp",EDGE,"E4");var subQ3=makeQuery(id+"F10.boolean.opBoolean","MERGE",FACE,{"derivedFrom":[makeQuery(id+"F6.boolean.opBoolean","MERGE",FACE,{"derivedFrom":[makeQuery(id+"F2.boolean.opBoolean","MERGE",FACE,{"derivedFrom":[makeQuery(id+"F1.opExtrude","CAP_FACE",FACE,{"disambiguationData":[OSD([sQuery(id+"F0.wireOp",EDGE,"E0"),sQuery(id+"F0.wireOp",EDGE,"E3"),subQ2,subQ1,sQuery(id+"F0.wireOp",EDGE,"E6"),sQuery(id+"F0.wireOp",EDGE,"E7"),sQuery(id+"F0.wireOp",EDGE,"E8"),sQuery(id+"F0.wireOp",EDGE,"E9")])],"isStart":false}),makeQuery(id+"F2.opExtrude","CAP_FACE",FACE,{"disambiguationData":[OSD([subQ2,sQuery(id+"F0.wireOp",EDGE,"E10"),sQuery(id+"F0.wireOp",EDGE,"E11"),sQuery(id+"F0.wireOp",EDGE,"E12")])],"isStart":false}),makeQuery(id+"F2.opExtrude","CAP_FACE",FACE,{"disambiguationData":[OSD([subQ1,sQuery(id+"F0.wireOp",EDGE,"E13"),subQ0,sQuery(id+"F0.wireOp",EDGE,"E15")])],"isStart":false})]}),makeQuery(id+"F6.opExtrude","SWEPT_FACE",FACE,{"disambiguationData":[OSD([sQuery(id+"F5.wireOp",EDGE,"E49.bottom")])]}),makeQuery(id+"F6.opExtrude","SWEPT_FACE",FACE,{"disambiguationData":[OSD([sQuery(id+"F5.wireOp",EDGE,"E50.bottom")])]}),makeQuery(id+"F6.opExtrude","SWEPT_FACE",FACE,{"disambiguationData":[OSD([sQuery(id+"F5.wireOp",EDGE,"E51.MirrorCS")])]}),makeQuery(id+"F6.opExtrude","SWEPT_FACE",FACE,{"disambiguationData":[OSD([sQuery(id+"F5.wireOp",EDGE,"E52.MirrorCS")])]}),makeQuery(id+"F6.opExtrude","SWEPT_FACE",FACE,{"disambiguationData":[OSD([sQuery(id+"F5.wireOp",EDGE,"E60.MirrorCS")])]}),makeQuery(id+"F6.opExtrude","SWEPT_FACE",FACE,{"disambiguationData":[OSD([sQuery(id+"F5.wireOp",EDGE,"E61.MirrorCS")])]})]}),makeQuery(id+"F10.opExtrude","SWEPT_FACE",FACE,{"disambiguationData":[OSD([sQuery(id+"F9.wireOp",EDGE,"E68.top")])]}),makeQuery(id+"F10.opExtrude","SWEPT_FACE",FACE,{"disambiguationData":[OSD([sQuery(id+"F9.wireOp",EDGE,"E69.top")])]})]});Q1=makeQuery(id+"F14.opChamfer","BLEND_EDGE",EDGE,{"blendedFrom":[makeQuery(id+"F13.opChamfer","BLEND_EDGE",EDGE,{"blendedFrom":[makeQuery(id+"F2.opExtrude","CAP_EDGE",EDGE,{"disambiguationData":[OSD([subQ0])],"isStart":false}),subQ3],"blendedInto":[subQ3]}),subQ3],"blendedInto":[subQ3]});}
            chamfer(context, id + "F15", {"entities" : qUnion([Q0, Q1]), "chamferType" : ChamferType.TWO_OFFSETS, "width1" : 12.7 * mm, "oppositeDirection" : false, "width2" : 5.08 * mm, "tangentPropagation" : true});
        }
    });
